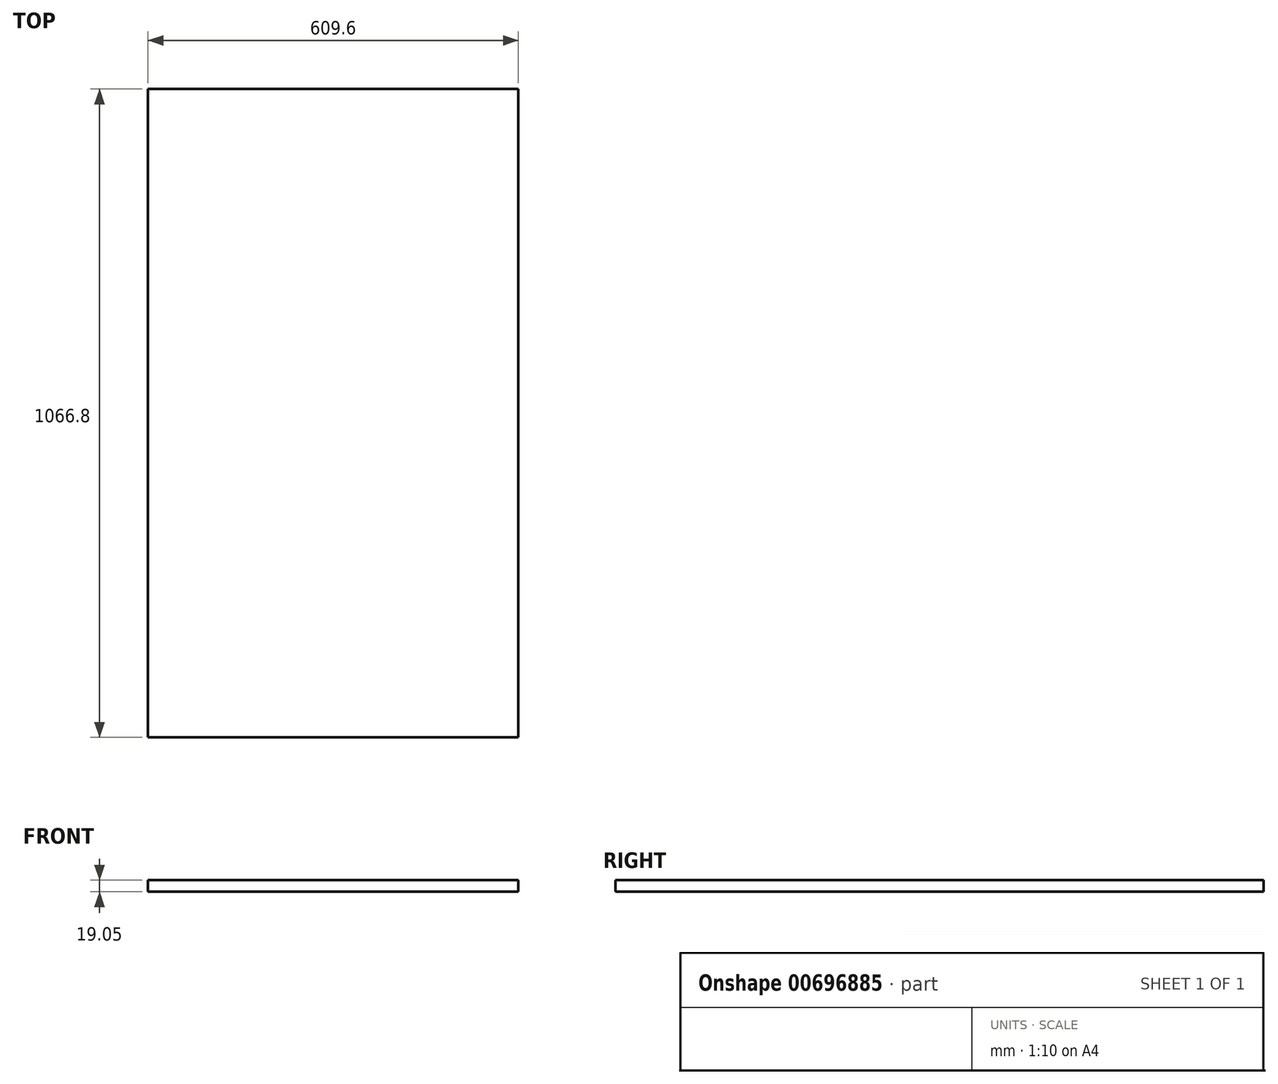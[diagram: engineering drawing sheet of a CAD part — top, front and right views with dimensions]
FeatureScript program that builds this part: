
annotation { "Feature Type Name" : "Feature", "Feature Type Description" : "" }
export const myFeature = defineFeature(function(context is Context, id is Id, definition is map)
    precondition{}
    {
        {
            var Q0;
            Q0=qCreatedBy(makeId("Top.planeOp"),FACE);
            var sketch = newSketch(context, id + "F0", { "sketchPlane" : qUnion([Q0])});
            skLineSegment(sketch, "E0.bottom", {"start": v(304.8, -533.4) * mm, "end": v(-304.8, -533.4) * mm});
            skLineSegment(sketch, "E0.top", {"start": v(304.8, 533.4) * mm, "end": v(-304.8, 533.4) * mm});
            skLineSegment(sketch, "E0.left", {"start": v(304.8, -533.4) * mm, "end": v(304.8, 533.4) * mm});
            skLineSegment(sketch, "E0.right", {"start": v(-304.8, -533.4) * mm, "end": v(-304.8, 533.4) * mm});
            skPoint(sketch, "E0.middle", {"position": v(0, 0) * mm});
            skSolve(sketch);
        }
        {
            var Q0;
            Q0=makeQuery(id+"F0.imprint","IMPRINT",FACE,{"disambiguationData":[TD([[makeQuery(id+"F0.imprint","IMPRINT",EDGE,{"derivedFrom":sQuery(id+"F0.wireOp",EDGE,"E0.bottom")}),-1.0]])]});
            extrude(context, id + "F1", {"entities" : qUnion([Q0]), "depth" : 19.05 * mm, "offsetDistance" : 25.4 * mm});
        }
    });
